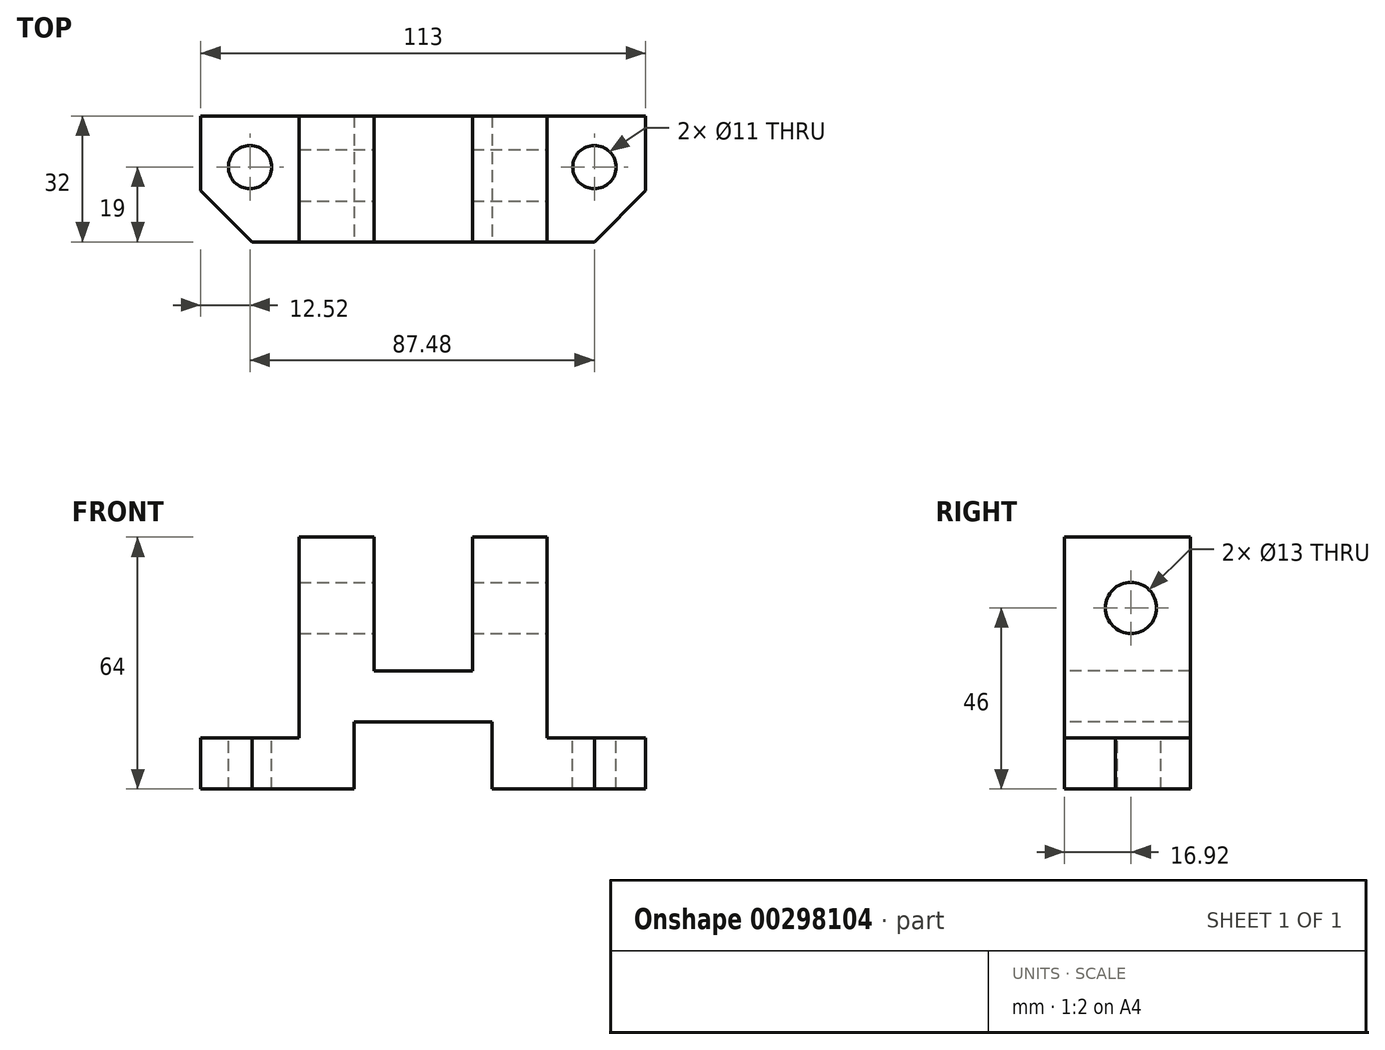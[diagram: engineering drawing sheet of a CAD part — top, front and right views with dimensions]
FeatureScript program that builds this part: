
annotation { "Feature Type Name" : "Feature", "Feature Type Description" : "" }
export const myFeature = defineFeature(function(context is Context, id is Id, definition is map)
    precondition{}
    {
        {
            var Q0;
            Q0=qCreatedBy(makeId("Front.planeOp"),FACE);
            var sketch = newSketch(context, id + "F0", { "sketchPlane" : qUnion([Q0])});
            skLineSegment(sketch, "E0.bottom", {"start": v(0, 0) * mm, "end": v(-113, 0) * mm});
            skLineSegment(sketch, "E0.top", {"start": v(0, -64) * mm, "end": v(-113, -64) * mm});
            skLineSegment(sketch, "E0.left", {"start": v(0, 0) * mm, "end": v(0, -64) * mm});
            skLineSegment(sketch, "E0.right", {"start": v(-113, 0) * mm, "end": v(-113, -64) * mm});
            skSolve(sketch);
        }
        {
            var Q0;
            Q0=makeQuery(id+"F0.imprint","IMPRINT",FACE,{"disambiguationData":[TD([[makeQuery(id+"F0.imprint","IMPRINT",EDGE,{"derivedFrom":sQuery(id+"F0.wireOp",EDGE,"E0.bottom")}),1.0]])]});
            extrude(context, id + "F1", {"entities" : qUnion([Q0]), "depth" : 32 * mm});
        }
        {
            var Q0;
            Q0=makeQuery(id+"F1.opExtrude","SWEPT_FACE",FACE,{"disambiguationData":[OSD([sQuery(id+"F0.wireOp",EDGE,"E0.left")])]});
            var sketch = newSketch(context, id + "F2", { "sketchPlane" : qUnion([Q0])});
            skLineSegment(sketch, "E1", {"start": v(0, 0) * mm, "end": v(-32, 0) * mm});
            skLineSegment(sketch, "E2", {"start": v(-32, 0) * mm, "end": v(-32, -51) * mm});
            skLineSegment(sketch, "E3", {"start": v(-32, -51) * mm, "end": v(0, -51) * mm});
            skLineSegment(sketch, "E4", {"start": v(0, -51) * mm, "end": v(0, 0) * mm});
            skSolve(sketch);
        }
        {
            var Q0;
            Q0=makeQuery(id+"F2.imprint","IMPRINT",FACE,{"disambiguationData":[TD([[makeQuery(id+"F2.imprint","IMPRINT",EDGE,{"derivedFrom":sQuery(id+"F2.wireOp",EDGE,"E1")}),-1.0]])]});
            extrude(context, id + "F3", {"entities" : qUnion([Q0]), "operationType" : NewBodyOperationType.REMOVE, "oppositeDirection" : true, "depth" : 25 * mm});
        }
        {
            var Q0;
            Q0=makeQuery(id+"F1.opExtrude","SWEPT_FACE",FACE,{"disambiguationData":[OSD([sQuery(id+"F0.wireOp",EDGE,"E0.right")])]});
            var sketch = newSketch(context, id + "F4", { "sketchPlane" : qUnion([Q0])});
            skLineSegment(sketch, "E5", {"start": v(0, 0) * mm, "end": v(32, 0) * mm});
            skLineSegment(sketch, "E6", {"start": v(32, 0) * mm, "end": v(32, -51) * mm});
            skLineSegment(sketch, "E7", {"start": v(32, -51) * mm, "end": v(0, -51) * mm});
            skLineSegment(sketch, "E8", {"start": v(0, -51) * mm, "end": v(0, 0) * mm});
            skSolve(sketch);
        }
        {
            var Q0;
            Q0=makeQuery(id+"F4.imprint","IMPRINT",FACE,{"disambiguationData":[TD([[makeQuery(id+"F4.imprint","IMPRINT",EDGE,{"derivedFrom":sQuery(id+"F4.wireOp",EDGE,"E5")}),1.0]])]});
            extrude(context, id + "F5", {"entities" : qUnion([Q0]), "operationType" : NewBodyOperationType.REMOVE, "oppositeDirection" : true, "depth" : 25 * mm});
        }
        {
            var Q0;
            Q0=makeQuery(id+"F1.opExtrude","CAP_FACE",FACE,{"disambiguationData":[OSD([sQuery(id+"F0.wireOp",EDGE,"E0.bottom"),sQuery(id+"F0.wireOp",EDGE,"E0.top"),sQuery(id+"F0.wireOp",EDGE,"E0.left"),sQuery(id+"F0.wireOp",EDGE,"E0.right")])],"isStart":false});
            var sketch = newSketch(context, id + "F6", { "sketchPlane" : qUnion([Q0])});
            skLineSegment(sketch, "E9", {"start": v(-56.5, -47) * mm, "end": v(-39, -47) * mm});
            skLineSegment(sketch, "E10", {"start": v(-39, -47) * mm, "end": v(-39, -64) * mm});
            skLineSegment(sketch, "E11", {"start": v(-39, -64) * mm, "end": v(-56.5, -64) * mm});
            skLineSegment(sketch, "E12", {"start": v(-56.5, -47) * mm, "end": v(-74, -47) * mm});
            skLineSegment(sketch, "E13", {"start": v(-74, -47) * mm, "end": v(-74, -64) * mm});
            skLineSegment(sketch, "E14", {"start": v(-74, -64) * mm, "end": v(-56.5, -64) * mm});
            skSolve(sketch);
        }
        {
            var Q0;
            Q0=makeQuery(id+"F6.imprint","IMPRINT",FACE,{"disambiguationData":[TD([[makeQuery(id+"F6.imprint","IMPRINT",EDGE,{"derivedFrom":sQuery(id+"F6.wireOp",EDGE,"E9")}),-1.0]])]});
            extrude(context, id + "F7", {"entities" : qUnion([Q0]), "operationType" : NewBodyOperationType.REMOVE, "endBound" : BoundingType.THROUGH_ALL, "oppositeDirection" : true, "depth" : 25 * mm});
        }
        {
            var Q0;
            Q0=makeQuery(id+"F1.opExtrude","CAP_FACE",FACE,{"disambiguationData":[OSD([sQuery(id+"F0.wireOp",EDGE,"E0.bottom"),sQuery(id+"F0.wireOp",EDGE,"E0.top"),sQuery(id+"F0.wireOp",EDGE,"E0.left"),sQuery(id+"F0.wireOp",EDGE,"E0.right")])],"isStart":false});
            var sketch = newSketch(context, id + "F8", { "sketchPlane" : qUnion([Q0])});
            skPoint(sketch, "E15.endSnap0", {"position": v(-56.5, 0) * mm});
            skLineSegment(sketch, "E16", {"start": v(-56.5, -34) * mm, "end": v(-44, -34) * mm});
            skLineSegment(sketch, "E17", {"start": v(-44, -34) * mm, "end": v(-44, 0) * mm});
            skLineSegment(sketch, "E18", {"start": v(-44, 0) * mm, "end": v(-56.5, 0) * mm});
            skLineSegment(sketch, "E19", {"start": v(-69, 0) * mm, "end": v(-69, -34) * mm});
            skLineSegment(sketch, "E20", {"start": v(-69, -34) * mm, "end": v(-56.5, -34) * mm});
            skLineSegment(sketch, "E21", {"start": v(-69, 0) * mm, "end": v(-56.5, 0) * mm});
            skSolve(sketch);
        }
        {
            var Q0;
            Q0=makeQuery(id+"F8.imprint","IMPRINT",FACE,{"disambiguationData":[TD([[makeQuery(id+"F8.imprint","IMPRINT",EDGE,{"derivedFrom":sQuery(id+"F8.wireOp",EDGE,"E16")}),1.0]])]});
            extrude(context, id + "F9", {"entities" : qUnion([Q0]), "operationType" : NewBodyOperationType.REMOVE, "endBound" : BoundingType.THROUGH_ALL, "oppositeDirection" : true, "depth" : 25 * mm});
        }
        {
            var Q0;
            Q0=makeQuery(id+"F1.opExtrude","CAP_EDGE",EDGE,{"disambiguationData":[OSD([sQuery(id+"F0.wireOp",EDGE,"E0.right")])],"isStart":false});
            chamfer(context, id + "F10", {"entities" : qUnion([Q0]), "width" : 13 * mm, "tangentPropagation" : true});
        }
        {
            var Q0;
            Q0=makeQuery(id+"F1.opExtrude","CAP_EDGE",EDGE,{"disambiguationData":[OSD([sQuery(id+"F0.wireOp",EDGE,"E0.left")])],"isStart":false});
            chamfer(context, id + "F11", {"entities" : qUnion([Q0]), "width" : 13 * mm, "tangentPropagation" : true});
        }
        {
            var Q0;
            Q0=makeQuery(id+"F3.boolean.opBoolean","COPY",FACE,{"derivedFrom":makeQuery(id+"F3.opExtrude","SWEPT_FACE",FACE,{"disambiguationData":[OSD([sQuery(id+"F2.wireOp",EDGE,"E3")])]})});
            var sketch = newSketch(context, id + "F12", { "sketchPlane" : qUnion([Q0])});
            skCircle(sketch, "E22", {"center": v(-13, -13) * mm, "radius": 5.5 * mm});
            skCircle(sketch, "E23", {"center": v(-100.48, -13) * mm, "radius": 5.5 * mm});
            skSolve(sketch);
        }
        {
            var Q0;
            Q0=makeQuery(id+"F12.imprint","IMPRINT",FACE,{"disambiguationData":[TD([[makeQuery(id+"F12.imprint","IMPRINT",EDGE,{"derivedFrom":sQuery(id+"F12.wireOp",EDGE,"E23")}),1.0]])]});
            var Q1;
            Q1=makeQuery(id+"F12.imprint","IMPRINT",FACE,{"disambiguationData":[TD([[makeQuery(id+"F12.imprint","IMPRINT",EDGE,{"derivedFrom":sQuery(id+"F12.wireOp",EDGE,"E22")}),1.0]])]});
            extrude(context, id + "F13", {"entities" : qUnion([Q0, Q1]), "operationType" : NewBodyOperationType.REMOVE, "endBound" : BoundingType.THROUGH_ALL, "oppositeDirection" : true, "depth" : 25 * mm});
        }
        {
            var Q0;
            Q0=makeQuery(id+"F3.boolean.opBoolean","COPY",FACE,{"derivedFrom":makeQuery(id+"F3.opExtrude","CAP_FACE",FACE,{"disambiguationData":[OSD([sQuery(id+"F2.wireOp",EDGE,"E1"),sQuery(id+"F2.wireOp",EDGE,"E2"),sQuery(id+"F2.wireOp",EDGE,"E3"),sQuery(id+"F2.wireOp",EDGE,"E4")])],"isStart":false})});
            var sketch = newSketch(context, id + "F14", { "sketchPlane" : qUnion([Q0])});
            skCircle(sketch, "E24", {"center": v(-15.08, -18) * mm, "radius": 6.5 * mm});
            skSolve(sketch);
        }
        {
            var Q0;
            Q0=makeQuery(id+"F14.imprint","IMPRINT",FACE,{"disambiguationData":[TD([[makeQuery(id+"F14.imprint","IMPRINT",EDGE,{"derivedFrom":sQuery(id+"F14.wireOp",EDGE,"E24")}),1.0]])]});
            extrude(context, id + "F15", {"entities" : qUnion([Q0]), "operationType" : NewBodyOperationType.REMOVE, "endBound" : BoundingType.THROUGH_ALL, "oppositeDirection" : true, "depth" : 25 * mm});
        }
    });
